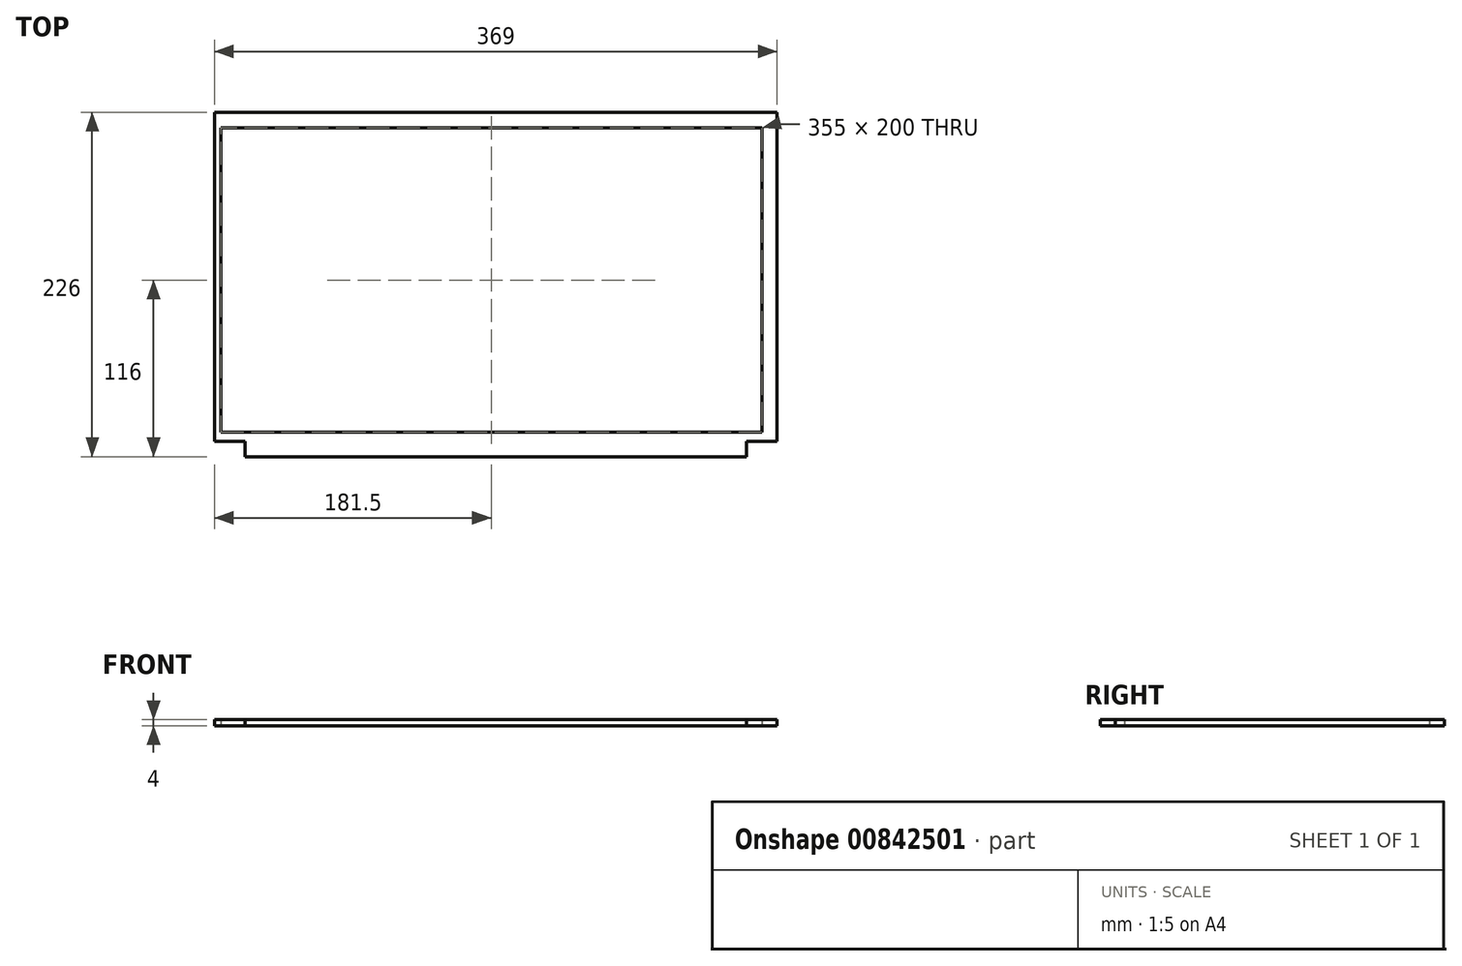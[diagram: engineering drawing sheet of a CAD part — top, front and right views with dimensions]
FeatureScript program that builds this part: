
annotation { "Feature Type Name" : "Feature", "Feature Type Description" : "" }
export const myFeature = defineFeature(function(context is Context, id is Id, definition is map)
    precondition{}
    {
        {
            var Q0;
            Q0=qCreatedBy(makeId("Top.planeOp"),FACE);
            var sketch = newSketch(context, id + "F0", { "sketchPlane" : qUnion([Q0])});
            skLineSegment(sketch, "E0.bottom", {"start": v(-180.5, 100) * mm, "end": v(174.5, 100) * mm});
            skLineSegment(sketch, "E0.top", {"start": v(-180.5, -100) * mm, "end": v(174.5, -100) * mm});
            skLineSegment(sketch, "E0.left", {"start": v(-180.5, 100) * mm, "end": v(-180.5, -100) * mm});
            skLineSegment(sketch, "E0.right", {"start": v(174.5, 100) * mm, "end": v(174.5, -100) * mm});
            skLineSegment(sketch, "E1.bottom", {"start": v(174.5, 100) * mm, "end": v(184.5, 100) * mm});
            skLineSegment(sketch, "E1.top", {"start": v(174.5, -100) * mm, "end": v(184.5, -100) * mm});
            skLineSegment(sketch, "E1.right", {"start": v(184.5, 100) * mm, "end": v(184.5, -100) * mm});
            skLineSegment(sketch, "E2.bottom", {"start": v(-180.5, -100) * mm, "end": v(-184.5, -100) * mm});
            skLineSegment(sketch, "E2.top", {"start": v(-180.5, 100) * mm, "end": v(-184.5, 100) * mm});
            skLineSegment(sketch, "E2.left", {"start": v(-180.5, -100) * mm, "end": v(-180.5, 100) * mm});
            skLineSegment(sketch, "E2.right", {"start": v(-184.5, -100) * mm, "end": v(-184.5, 100) * mm});
            skLineSegment(sketch, "E3.bottom", {"start": v(-184.5, 100) * mm, "end": v(184.5, 100) * mm});
            skLineSegment(sketch, "E3.top", {"start": v(-184.5, 110) * mm, "end": v(184.5, 110) * mm});
            skLineSegment(sketch, "E3.left", {"start": v(-184.5, 100) * mm, "end": v(-184.5, 110) * mm});
            skLineSegment(sketch, "E3.right", {"start": v(184.5, 100) * mm, "end": v(184.5, 110) * mm});
            skLineSegment(sketch, "E4.bottom", {"start": v(-184.5, -100) * mm, "end": v(184.5, -100) * mm});
            skLineSegment(sketch, "E4.top", {"start": v(-184.5, -106) * mm, "end": v(184.5, -106) * mm});
            skLineSegment(sketch, "E4.left", {"start": v(-184.5, -100) * mm, "end": v(-184.5, -106) * mm});
            skLineSegment(sketch, "E4.right", {"start": v(184.5, -100) * mm, "end": v(184.5, -106) * mm});
            skLineSegment(sketch, "E5.bottom", {"start": v(-164.5, -106) * mm, "end": v(164.5, -106) * mm});
            skLineSegment(sketch, "E5.top", {"start": v(-164.5, -116) * mm, "end": v(164.5, -116) * mm});
            skLineSegment(sketch, "E5.left", {"start": v(-164.5, -106) * mm, "end": v(-164.5, -116) * mm});
            skLineSegment(sketch, "E5.right", {"start": v(164.5, -106) * mm, "end": v(164.5, -116) * mm});
            skLineSegment(sketch, "E6", {"start": v(-164.5, -116) * mm, "end": v(-184.5, -116) * mm, "construction": true});
            skLineSegment(sketch, "E7", {"start": v(-184.5, -116) * mm, "end": v(-184.5, -106) * mm, "construction": true});
            skLineSegment(sketch, "E8", {"start": v(164.5, -116) * mm, "end": v(184.5, -116) * mm, "construction": true});
            skLineSegment(sketch, "E9", {"start": v(184.5, -116) * mm, "end": v(184.5, -106) * mm, "construction": true});
            skLineSegment(sketch, "E10", {"start": v(0, 100) * mm, "end": v(0, -100) * mm, "construction": true});
            skLineSegment(sketch, "E11", {"start": v(0, 0) * mm, "end": v(-180.5, 0) * mm, "construction": true});
            skSolve(sketch);
        }
        {
            var Q0;
            Q0=makeQuery(id+"F0.imprint","IMPRINT",FACE,{"disambiguationData":[TD([[makeQuery(id+"F0.imprint","IMPRINT",EDGE,{"derivedFrom":sQuery(id+"F0.wireOp",EDGE,"E0.bottom")}),1.0]])]});
            var Q1;
            Q1=makeQuery(id+"F0.imprint","IMPRINT",FACE,{"disambiguationData":[TD([[makeQuery(id+"F0.imprint","IMPRINT",EDGE,{"derivedFrom":sQuery(id+"F0.wireOp",EDGE,"E0.left")}),-1.0]])]});
            var Q2;
            Q2=makeQuery(id+"F0.imprint","IMPRINT",FACE,{"disambiguationData":[TD([[makeQuery(id+"F0.imprint","IMPRINT",EDGE,{"derivedFrom":sQuery(id+"F0.wireOp",EDGE,"E0.top")}),-1.0]])]});
            var Q3;
            Q3=makeQuery(id+"F0.imprint","IMPRINT",FACE,{"disambiguationData":[TD([[makeQuery(id+"F0.imprint","IMPRINT",EDGE,{"derivedFrom":sQuery(id+"F0.wireOp",EDGE,"E5.top")}),1.0]])]});
            var Q4;
            Q4=makeQuery(id+"F0.imprint","IMPRINT",FACE,{"disambiguationData":[TD([[makeQuery(id+"F0.imprint","IMPRINT",EDGE,{"derivedFrom":sQuery(id+"F0.wireOp",EDGE,"E0.right")}),1.0]])]});
            extrude(context, id + "F1", {"entities" : qUnion([Q0, Q1, Q2, Q3, Q4]), "depth" : 4 * mm, "offsetDistance" : 25 * mm});
        }
        {
            var Q0;
            Q0=makeQuery(id+"F1.opExtrude","CAP_FACE",FACE,{"disambiguationData":[OSD([sQuery(id+"F0.wireOp",EDGE,"E0.bottom"),sQuery(id+"F0.wireOp",EDGE,"E0.top"),sQuery(id+"F0.wireOp",EDGE,"E0.left"),sQuery(id+"F0.wireOp",EDGE,"E0.right"),sQuery(id+"F0.wireOp",EDGE,"E1.right"),sQuery(id+"F0.wireOp",EDGE,"E2.right"),sQuery(id+"F0.wireOp",EDGE,"E3.top"),sQuery(id+"F0.wireOp",EDGE,"E3.left"),sQuery(id+"F0.wireOp",EDGE,"E3.right"),sQuery(id+"F0.wireOp",EDGE,"E4.top"),sQuery(id+"F0.wireOp",EDGE,"E4.left"),sQuery(id+"F0.wireOp",EDGE,"E4.right"),sQuery(id+"F0.wireOp",EDGE,"E5.top"),sQuery(id+"F0.wireOp",EDGE,"E5.left"),sQuery(id+"F0.wireOp",EDGE,"E5.right")])],"isStart":true});
            var sketch = newSketch(context, id + "F2", { "sketchPlane" : qUnion([Q0])});
            skLineSegment(sketch, "E12.bottom", {"start": v(174.5, 100) * mm, "end": v(-180.5, 100) * mm});
            skLineSegment(sketch, "E12.top", {"start": v(174.5, -100) * mm, "end": v(-180.5, -100) * mm});
            skLineSegment(sketch, "E12.left", {"start": v(174.5, 100) * mm, "end": v(174.5, -100) * mm});
            skLineSegment(sketch, "E12.right", {"start": v(-180.5, 100) * mm, "end": v(-180.5, -100) * mm});
            skSolve(sketch);
        }
        {
            var Q0;
            Q0=makeQuery(id+"F2.imprint","IMPRINT",FACE,{"disambiguationData":[TD([[makeQuery(id+"F2.imprint","IMPRINT",EDGE,{"derivedFrom":sQuery(id+"F2.wireOp",EDGE,"E12.bottom")}),-1.0]])]});
            extrude(context, id + "F3", {"entities" : qUnion([Q0]), "oppositeDirection" : true, "depth" : 4 * mm, "offsetDistance" : 25 * mm});
        }
    });
